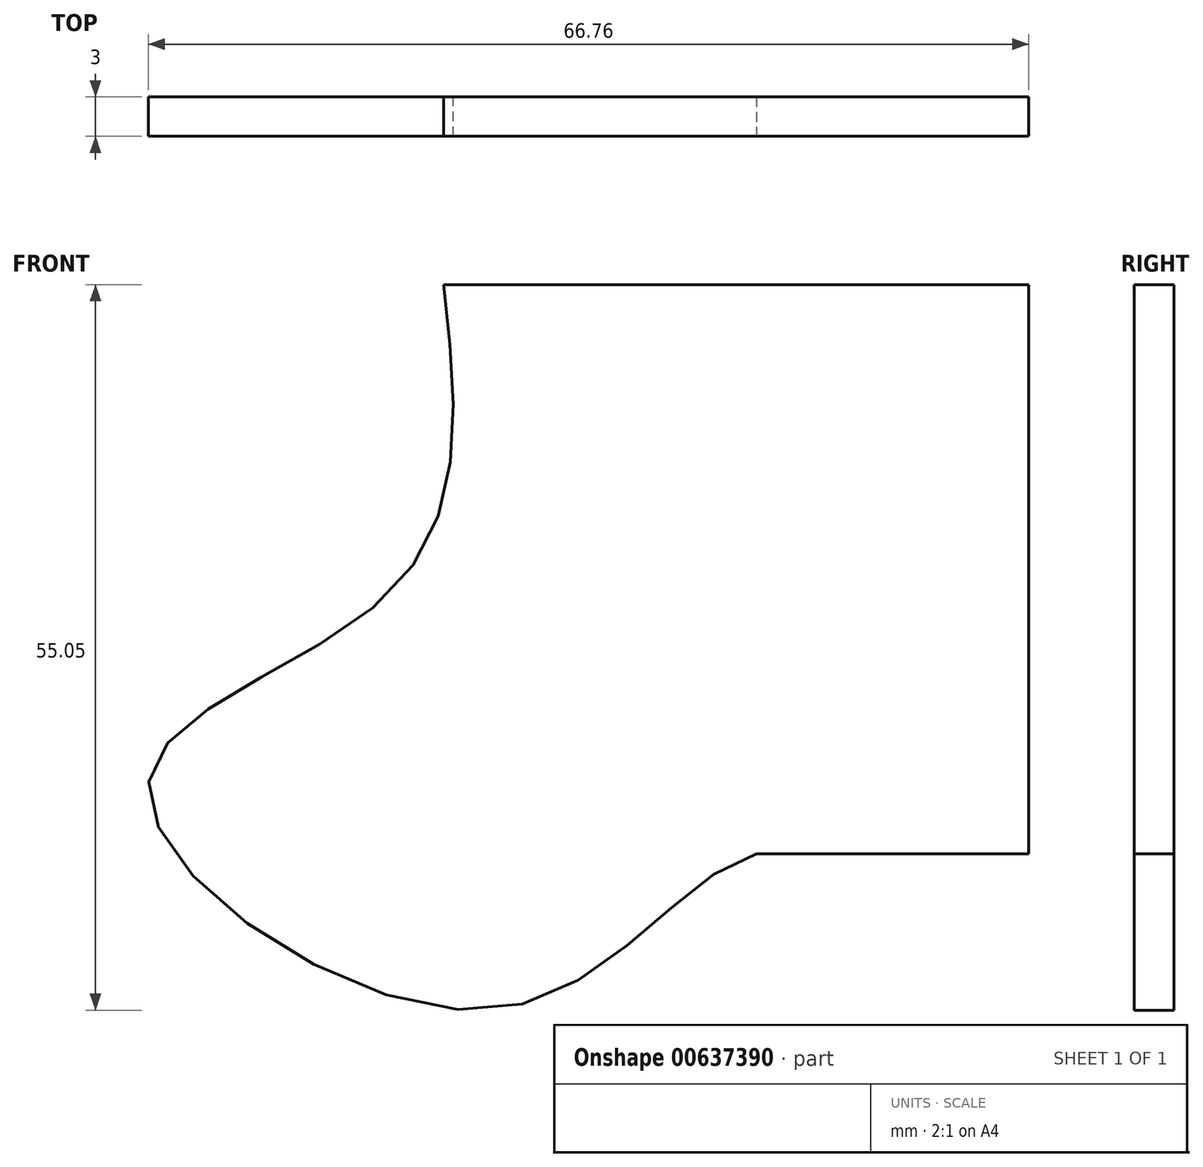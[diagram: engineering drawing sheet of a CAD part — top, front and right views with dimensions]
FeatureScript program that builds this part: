
annotation { "Feature Type Name" : "Feature", "Feature Type Description" : "" }
export const myFeature = defineFeature(function(context is Context, id is Id, definition is map)
    precondition{}
    {
        {
            assignVariable(context, id + "F0", {"name" : "gary", "anyValue" : 3});
        }
        {
            var Q0;
            Q0=qCreatedBy(makeId("Front.planeOp"),FACE);
            var sketch = newSketch(context, id + "F1", { "sketchPlane" : qUnion([Q0])});
            skLineSegment(sketch, "E0.bottom", {"start": v(38.1, 38.1) * mm, "end": v(-38.1, 38.1) * mm});
            skLineSegment(sketch, "E0.top", {"start": v(38.1, -38.1) * mm, "end": v(-38.1, -38.1) * mm});
            skLineSegment(sketch, "E0.left", {"start": v(38.1, 38.1) * mm, "end": v(38.1, -38.1) * mm});
            skLineSegment(sketch, "E0.right", {"start": v(-38.1, 38.1) * mm, "end": v(-38.1, -38.1) * mm});
            skPoint(sketch, "E0.middle", {"position": v(0, 0) * mm});
            skSolve(sketch);
        }
        {
            var Q0;
            Q0=makeQuery(id+"F1.imprint","IMPRINT",FACE,{"disambiguationData":[TD([[makeQuery(id+"F1.imprint","IMPRINT",EDGE,{"derivedFrom":sQuery(id+"F1.wireOp",EDGE,"E0.bottom")}),1.0]])]});
            extrude(context, id + "F2", {"entities" : qUnion([Q0]), "depth" : (getVariable(context, 'gary')) * mm, "offsetDistance" : 25.4 * mm});
        }
        {
            var Q0;
            Q0=makeQuery(id+"F2.opExtrude","CAP_FACE",FACE,{"disambiguationData":[OSD([sQuery(id+"F1.wireOp",EDGE,"E0.bottom"),sQuery(id+"F1.wireOp",EDGE,"E0.top"),sQuery(id+"F1.wireOp",EDGE,"E0.left"),sQuery(id+"F1.wireOp",EDGE,"E0.right")])],"isStart":false});
            var sketch = newSketch(context, id + "F3", { "sketchPlane" : qUnion([Q0])});
            skFitSpline(sketch, "E1", {"points": [v(-6.28, 38.1) * mm, v(-10, 15.07) * mm, v(-28.66, 0) * mm, v(-2.81, -16.9) * mm, v(17.44, -5.08) * mm], "startDerivative": vector(11.93, -104.38) * mm, "endDerivative": vector(75.73, 20.96) * mm});
            skLineSegment(sketch, "E2", {"start": v(17.44, -5.08) * mm, "end": v(38.1, -5.08) * mm});
            skSolve(sketch);
        }
        {
            var Q0;
            {var subQ3=sQuery(id+"F3.wireOp",EDGE,"E1");Q0=makeQuery(id+"F3.imprint","IMPRINT",FACE,{"disambiguationData":[TD([[makeQuery(id+"F3.imprint","IMPRINT",EDGE,{"derivedFrom":subQ3}),-1.0]])]});}
            extrude(context, id + "F4", {"entities" : qUnion([Q0]), "operationType" : NewBodyOperationType.REMOVE, "oppositeDirection" : true, "depth" : (getVariable(context, 'gary')) * mm, "offsetDistance" : 25.4 * mm});
        }
    });
